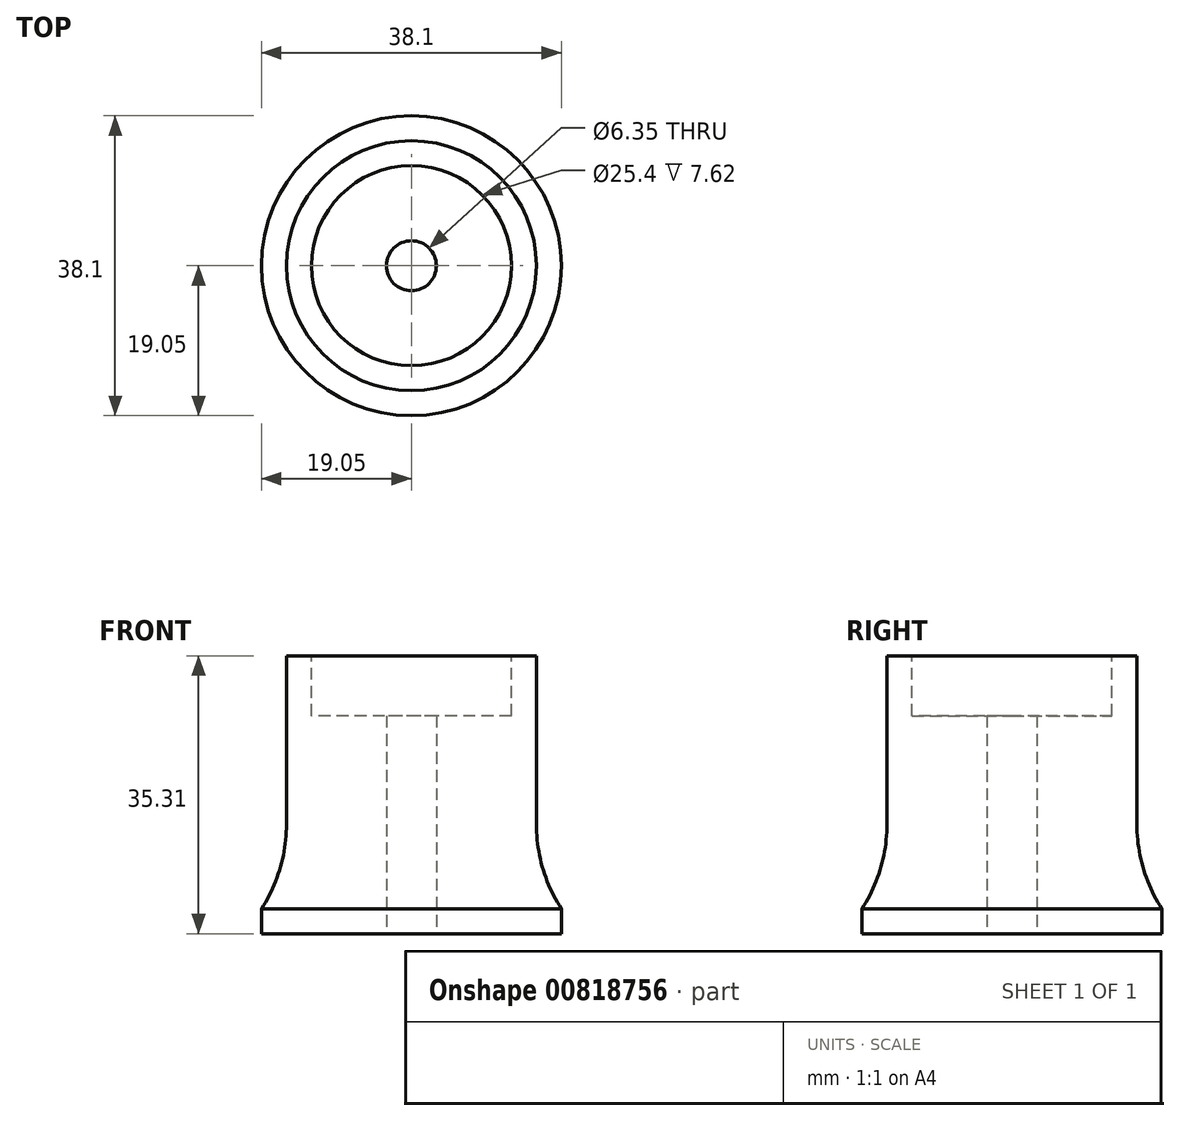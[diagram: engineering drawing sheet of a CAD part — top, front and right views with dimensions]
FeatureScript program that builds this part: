
annotation { "Feature Type Name" : "Feature", "Feature Type Description" : "" }
export const myFeature = defineFeature(function(context is Context, id is Id, definition is map)
    precondition{}
    {
        {
            var Q0;
            Q0=qCreatedBy(makeId("Front.planeOp"),FACE);
            var sketch = newSketch(context, id + "F0", { "sketchPlane" : qUnion([Q0])});
            skLineSegment(sketch, "E0", {"start": v(3.17, 35.3) * mm, "end": v(15.87, 35.3) * mm});
            skLineSegment(sketch, "E1", {"start": v(3.18, 0) * mm, "end": v(19.05, 0) * mm});
            skLineSegment(sketch, "E2", {"start": v(19.05, 0) * mm, "end": v(19.05, 3.18) * mm});
            skArc(sketch, "E3", {"start": v(15.87, 13.9) * mm, "mid": v(16.69, 8.3) * mm, "end": v(19.05, 3.18) * mm});
            skLineSegment(sketch, "E4", {"start": v(3.17, 35.3) * mm, "end": v(3.18, 0) * mm});
            skPoint(sketch, "E5.orphan", {"position": v(0, 35.3) * mm});
            skLineSegment(sketch, "E6", {"start": v(0, 0) * mm, "end": v(0, 52.88) * mm, "construction": true});
            skLineSegment(sketch, "E7", {"start": v(15.87, 13.9) * mm, "end": v(15.87, 35.3) * mm});
            skSolve(sketch);
        }
        {
            var Q0;
            Q0=makeQuery(id+"F0.imprint","IMPRINT",FACE,{"disambiguationData":[TD([[makeQuery(id+"F0.imprint","IMPRINT",EDGE,{"derivedFrom":sQuery(id+"F0.wireOp",EDGE,"E0")}),-1.0]])]});
            var Q1;
            Q1=sQuery(id+"F0.wireOp",EDGE,"E6");
            revolve(context, id + "F1", {"surfaceOperationType" : NewSurfaceOperationType.NEW, "entities" : qUnion([Q0]), "axis" : qUnion([Q1]), "revolveType" : RevolveType.FULL});
        }
        {
            var Q0;
            Q0=makeQuery(id+"F1.opRevolve","SWEPT_FACE",FACE,{"disambiguationData":[OSD([sQuery(id+"F0.wireOp",EDGE,"E0")])]});
            var sketch = newSketch(context, id + "F2", { "sketchPlane" : qUnion([Q0])});
            skCircle(sketch, "E8", {"center": v(0, 0) * mm, "radius": 12.7 * mm});
            skSolve(sketch);
        }
        {
            var Q0;
            Q0 = qSketchRegion(id + "F2", true);
            extrude(context, id + "F3", {"entities" : qUnion([Q0]), "operationType" : NewBodyOperationType.REMOVE, "oppositeDirection" : true, "depth" : 7.62 * mm, "offsetDistance" : 25.4 * mm});
        }
    });
